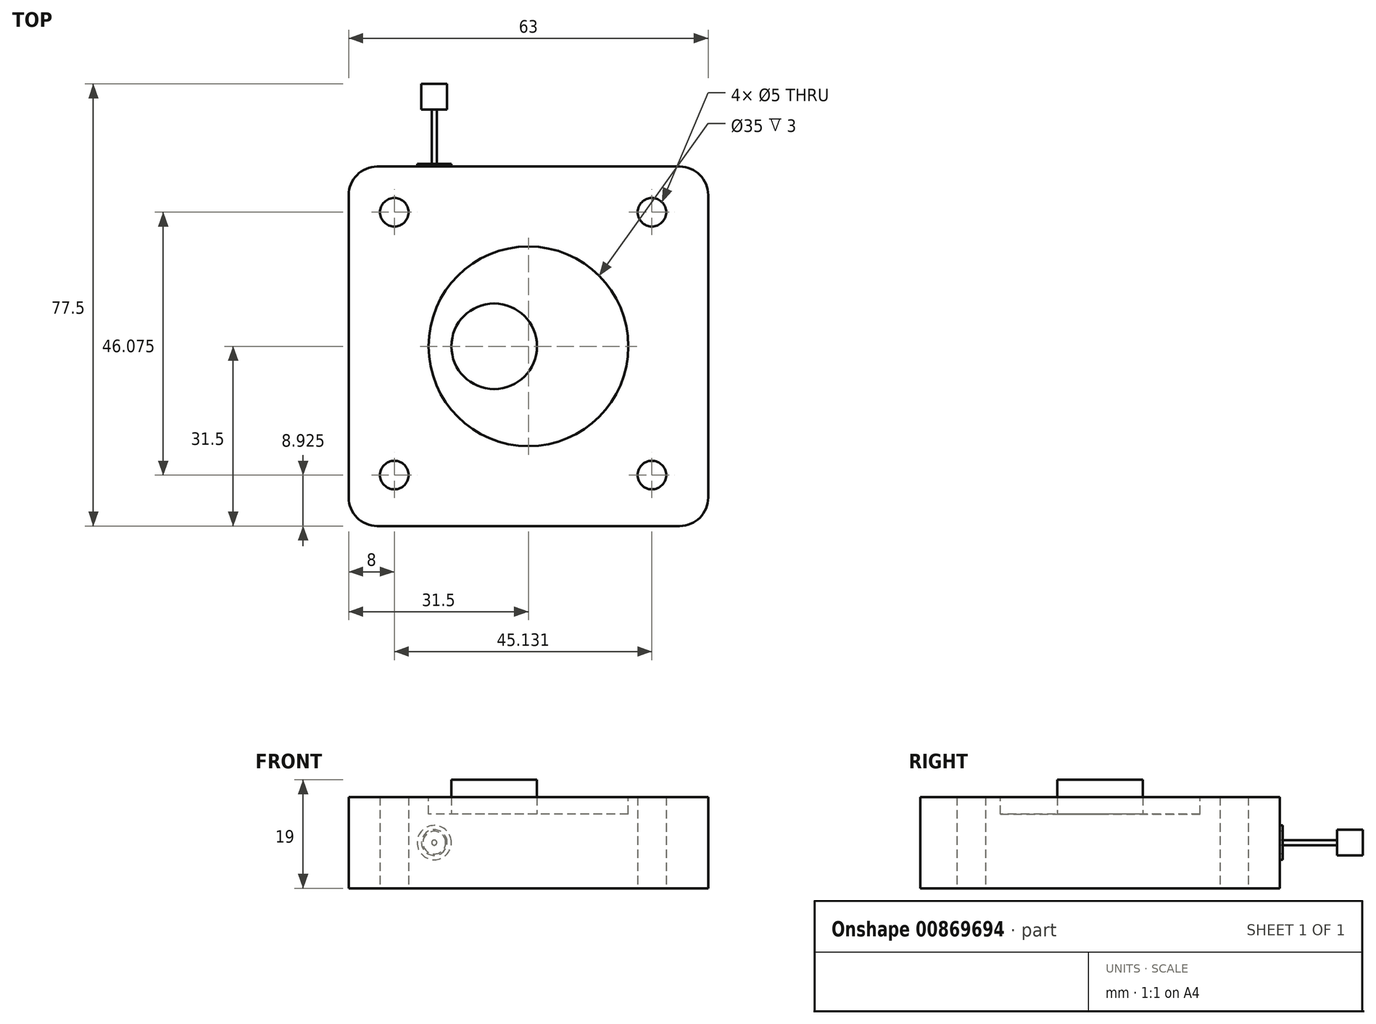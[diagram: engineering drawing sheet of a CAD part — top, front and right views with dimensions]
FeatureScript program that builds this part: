
annotation { "Feature Type Name" : "Feature", "Feature Type Description" : "" }
export const myFeature = defineFeature(function(context is Context, id is Id, definition is map)
    precondition{}
    {
        {
            var Q0;
            Q0=qCreatedBy(makeId("Top.planeOp"),FACE);
            var sketch = newSketch(context, id + "F0", { "sketchPlane" : qUnion([Q0])});
            skLineSegment(sketch, "E0.bottom", {"start": v(26.5, -31.5) * mm, "end": v(-26.5, -31.5) * mm});
            skLineSegment(sketch, "E0.top", {"start": v(26.5, 31.5) * mm, "end": v(-26.5, 31.5) * mm});
            skLineSegment(sketch, "E0.left", {"start": v(31.5, -26.5) * mm, "end": v(31.5, 26.5) * mm});
            skLineSegment(sketch, "E0.right", {"start": v(-31.5, -26.5) * mm, "end": v(-31.5, 26.5) * mm});
            skPoint(sketch, "E0.middle", {"position": v(0, 0) * mm});
            skPoint(sketch, "E1.visualSharp", {"position": v(-31.5, 31.5) * mm});
            skArc(sketch, "E1.filletArc", {"start": v(-26.5, 31.5) * mm, "mid": v(-30.04, 30.04) * mm, "end": v(-31.5, 26.5) * mm});
            skPoint(sketch, "E2.visualSharp", {"position": v(31.5, 31.5) * mm});
            skArc(sketch, "E2.filletArc", {"start": v(31.5, 26.5) * mm, "mid": v(30.04, 30.04) * mm, "end": v(26.5, 31.5) * mm});
            skPoint(sketch, "E3.visualSharp", {"position": v(31.5, -31.5) * mm});
            skArc(sketch, "E3.filletArc", {"start": v(26.5, -31.5) * mm, "mid": v(30.04, -30.04) * mm, "end": v(31.5, -26.5) * mm});
            skPoint(sketch, "E4.visualSharp", {"position": v(-31.5, -31.5) * mm});
            skArc(sketch, "E4.filletArc", {"start": v(-31.5, -26.5) * mm, "mid": v(-30.04, -30.04) * mm, "end": v(-26.5, -31.5) * mm});
            skCircle(sketch, "E5", {"center": v(-23.5, 23.5) * mm, "radius": 2.5 * mm});
            skCircle(sketch, "E6", {"center": v(21.63, 23.5) * mm, "radius": 2.5 * mm});
            skCircle(sketch, "E7", {"center": v(21.63, -22.58) * mm, "radius": 2.5 * mm});
            skCircle(sketch, "E8", {"center": v(-23.5, -22.58) * mm, "radius": 2.5 * mm});
            skSolve(sketch);
        }
        {
            var Q0;
            Q0=qSketchRegion(id+"F0",true);
            extrude(context, id + "F1", {"entities" : qUnion([Q0]), "depth" : 16 * mm, "offsetDistance" : 25 * mm});
        }
        {
            var Q0;
            Q0=makeQuery(id+"F1.opExtrude","CAP_FACE",FACE,{"disambiguationData":[OSD([sQuery(id+"F0.wireOp",EDGE,"E0.bottom"),sQuery(id+"F0.wireOp",EDGE,"E0.top"),sQuery(id+"F0.wireOp",EDGE,"E0.left"),sQuery(id+"F0.wireOp",EDGE,"E0.right"),sQuery(id+"F0.wireOp",EDGE,"E1.filletArc"),sQuery(id+"F0.wireOp",EDGE,"E2.filletArc"),sQuery(id+"F0.wireOp",EDGE,"E3.filletArc"),sQuery(id+"F0.wireOp",EDGE,"E4.filletArc"),sQuery(id+"F0.wireOp",EDGE,"E5"),sQuery(id+"F0.wireOp",EDGE,"E6"),sQuery(id+"F0.wireOp",EDGE,"E7"),sQuery(id+"F0.wireOp",EDGE,"E8")])],"isStart":false});
            var sketch = newSketch(context, id + "F2", { "sketchPlane" : qUnion([Q0])});
            skCircle(sketch, "E9", {"center": v(0, 0) * mm, "radius": 17.5 * mm});
            skSolve(sketch);
        }
        {
            var Q0;
            Q0=qSketchRegion(id+"F2",true);
            extrude(context, id + "F3", {"entities" : qUnion([Q0]), "operationType" : NewBodyOperationType.REMOVE, "oppositeDirection" : true, "depth" : 3 * mm, "offsetDistance" : 25 * mm});
        }
        {
            var Q0;
            Q0=makeQuery(id+"F3.boolean.opBoolean","COPY",FACE,{"derivedFrom":makeQuery(id+"F3.opExtrude","CAP_FACE",FACE,{"disambiguationData":[OSD([sQuery(id+"F2.wireOp",EDGE,"E9")])],"isStart":false})});
            var sketch = newSketch(context, id + "F4", { "sketchPlane" : qUnion([Q0])});
            skCircle(sketch, "E10", {"center": v(-6, 0) * mm, "radius": 7.5 * mm});
            skSolve(sketch);
        }
        {
            var Q0;
            Q0=qSketchRegion(id+"F4",true);
            extrude(context, id + "F5", {"entities" : qUnion([Q0]), "depth" : 6 * mm, "offsetDistance" : 25 * mm});
        }
        {
            var Q0;
            Q0=makeQuery(id+"F1.opExtrude","SWEPT_FACE",FACE,{"disambiguationData":[OSD([sQuery(id+"F0.wireOp",EDGE,"E0.top")])]});
            var sketch = newSketch(context, id + "F6", { "sketchPlane" : qUnion([Q0])});
            skCircle(sketch, "E11", {"center": v(16.5, 8) * mm, "radius": 2 * mm});
            skCircle(sketch, "E12", {"center": v(16.5, 8) * mm, "radius": 3 * mm});
            skLineSegment(sketch, "E13", {"start": v(16.5, 16) * mm, "end": v(16.5, 0) * mm});
            skSolve(sketch);
        }
        {
            var Q0;
            Q0=qSketchRegion(id+"F6",true);
            extrude(context, id + "F7", {"entities" : qUnion([Q0]), "operationType" : NewBodyOperationType.ADD, "depth" : .5 * mm, "offsetDistance" : 25 * mm});
        }
        {
            var Q0;
            Q0=makeQuery(id+"F7.boolean.opBoolean","SPLIT",FACE,{"disambiguationData":[TD([makeQuery(id+"F7.opExtrude","SWEPT_FACE",FACE,{"disambiguationData":[OSD([sQuery(id+"F6.wireOp",EDGE,"E11")])]})])],"derivedFrom":makeQuery(id+"F1.opExtrude","SWEPT_FACE",FACE,{"disambiguationData":[OSD([sQuery(id+"F0.wireOp",EDGE,"E0.top")])]})});
            var sketch = newSketch(context, id + "F8", { "sketchPlane" : qUnion([Q0])});
            skCircle(sketch, "E14", {"center": v(16.5, 8) * mm, "radius": 0.45 * mm});
            skSolve(sketch);
        }
        {
            var Q0;
            Q0=qSketchRegion(id+"F8",true);
            extrude(context, id + "F9", {"entities" : qUnion([Q0]), "operationType" : NewBodyOperationType.ADD, "depth" : 10 * mm, "offsetDistance" : 25 * mm});
        }
        {
            var Q0;
            Q0=makeQuery(id+"F9.opExtrude","CAP_FACE",FACE,{"disambiguationData":[OSD([sQuery(id+"F8.wireOp",EDGE,"E14")])],"isStart":false});
            var sketch = newSketch(context, id + "F10", { "sketchPlane" : qUnion([Q0])});
            skCircle(sketch, "E15", {"center": v(16.5, 8) * mm, "radius": 2.25 * mm});
            skSolve(sketch);
        }
        {
            var Q0;
            Q0=qSketchRegion(id+"F10",true);
            extrude(context, id + "F11", {"entities" : qUnion([Q0]), "operationType" : NewBodyOperationType.ADD, "depth" : 4.5 * mm, "offsetDistance" : 25 * mm});
        }
    });
